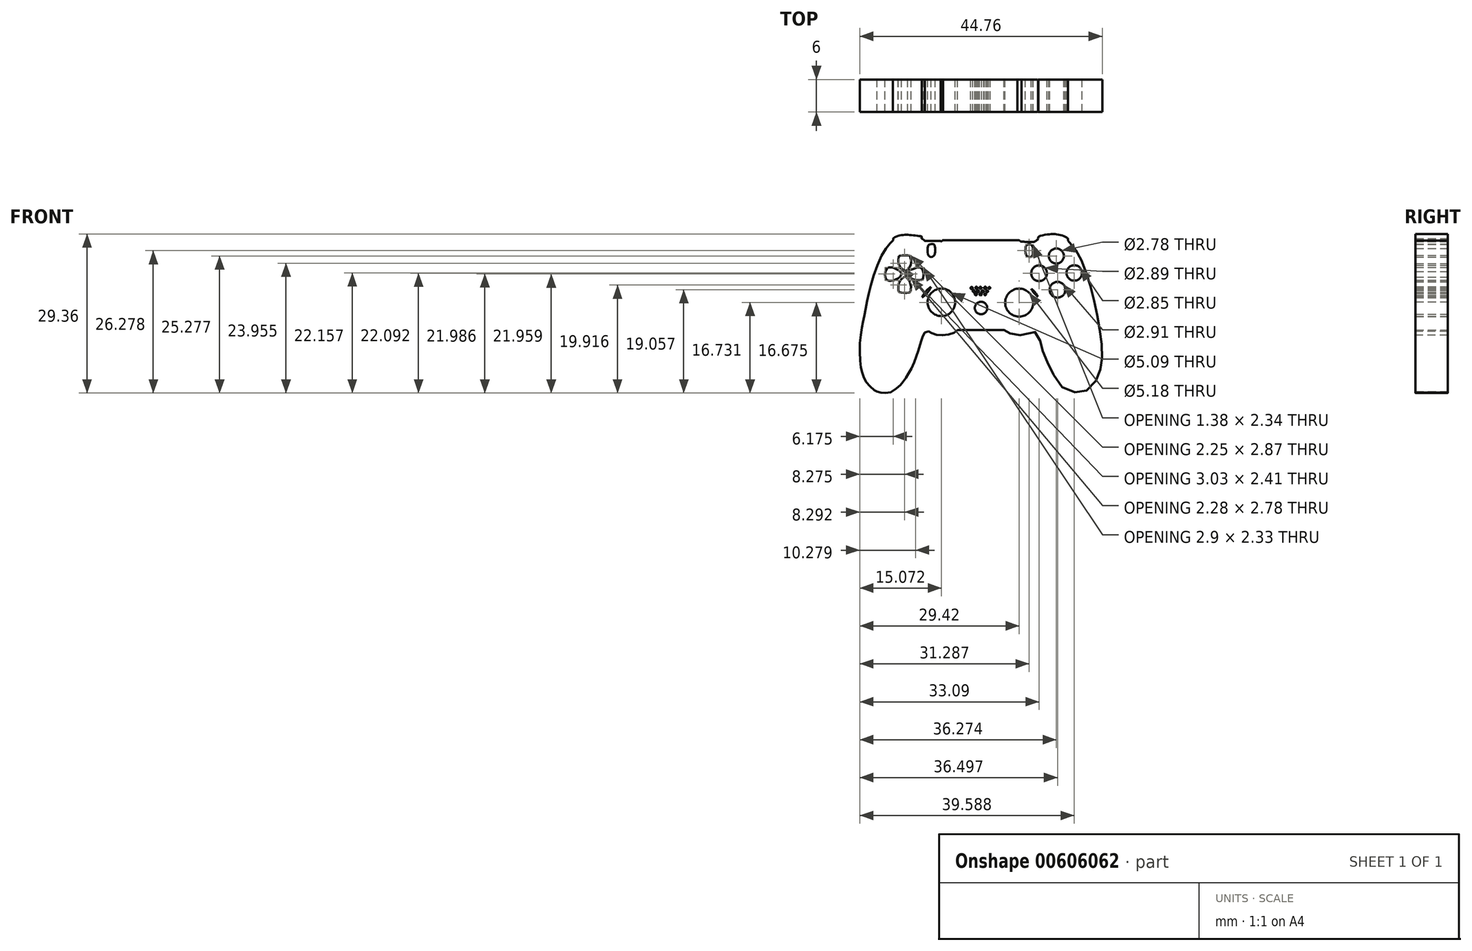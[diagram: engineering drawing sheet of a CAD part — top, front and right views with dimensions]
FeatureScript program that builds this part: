
annotation { "Feature Type Name" : "Feature", "Feature Type Description" : "" }
export const myFeature = defineFeature(function(context is Context, id is Id, definition is map)
    precondition{}
    {
        {
            var Q0;
            Q0=qCreatedBy(makeId("Front.planeOp"),FACE);
            var sketch = newSketch(context, id + "F0", { "sketchPlane" : qUnion([Q0])});
            skFitSpline(sketch, "E0", {"points": [v(11.67, 8.48) * mm, v(11.11, 8.8) * mm, v(9.77, 10.08) * mm, v(9.07, 11.57) * mm, v(8.73, 12.76) * mm, v(8.47, 16.23) * mm, v(8.78, 19.97) * mm, v(9.18, 21.94) * mm, v(9.76, 24.84) * mm, v(10.63, 28.56) * mm, v(12.8, 34.17) * mm, v(14.32, 36.12) * mm, v(14.98, 36.64) * mm, v(16, 37) * mm, v(17.62, 37.09) * mm, v(19.46, 36.87) * mm, v(20.12, 36.63) * mm, v(20.5, 36.3) * mm], "startDerivative": vector(-18.45, 2.92) * mm, "endDerivative": vector(11.5, -12.44) * mm});
            skFitSpline(sketch, "E1", {"points": [v(20.5, 36.3) * mm, v(23.4, 36.3) * mm], "startDerivative": vector(3.01, 0) * mm, "endDerivative": vector(3.01, 0) * mm});
            skFitSpline(sketch, "E2", {"points": [v(23.4, 36.3) * mm, v(23.82, 36.46) * mm], "startDerivative": vector(0.4, -0.48) * mm, "endDerivative": vector(0.31, 0.18) * mm});
            skLineSegment(sketch, "E3", {"start": v(23.82, 36.46) * mm, "end": v(37.6, 36.46) * mm});
            skFitSpline(sketch, "E4", {"points": [v(37.6, 36.46) * mm, v(38.35, 36.22) * mm], "startDerivative": vector(1.6, 0.03) * mm, "endDerivative": vector(1.1, 0.2) * mm});
            skFitSpline(sketch, "E5", {"points": [v(38.35, 36.22) * mm, v(40.82, 36.22) * mm, v(41.45, 36.68) * mm, v(43.77, 37.02) * mm, v(46.14, 36.77) * mm, v(47.69, 35.64) * mm, v(48.65, 34.04) * mm, v(49.36, 32.8) * mm, v(50.13, 30.79) * mm, v(50.8, 28.81) * mm, v(51.51, 26.15) * mm, v(52.19, 23.38) * mm, v(52.54, 21.15) * mm, v(52.94, 18.57) * mm, v(53.22, 16.06) * mm, v(53.13, 13.9) * mm, v(52.85, 12.5) * mm, v(52.31, 10.95) * mm, v(50.93, 9.07) * mm, v(49.41, 8.37) * mm, v(47.47, 8.5) * mm, v(45.46, 9.67) * mm, v(44.05, 11.97) * mm, v(43.06, 14.05) * mm, v(42.43, 15.53) * mm, v(42, 16.9) * mm, v(41.62, 18.35) * mm, v(40.95, 19.41) * mm, v(40.55, 19.61) * mm, v(40.08, 19.46) * mm, v(39.08, 19.02) * mm, v(38.35, 18.91) * mm, v(37.21, 18.94) * mm, v(36.04, 19.31) * mm, v(35.5, 19.52) * mm, v(35.06, 19.9) * mm], "startDerivative": vector(85.73, -8.47) * mm, "endDerivative": vector(-25.77, 24.87) * mm});
            skLineSegment(sketch, "E6", {"start": v(35.06, 19.9) * mm, "end": v(26.53, 19.9) * mm});
            skFitSpline(sketch, "E7", {"points": [v(26.53, 19.9) * mm, v(25.8, 19.32) * mm, v(24.43, 18.94) * mm, v(22.8, 18.95) * mm, v(21.78, 19.28) * mm, v(21.27, 19.58) * mm, v(20.71, 19.6) * mm, v(20.21, 19) * mm, v(19.94, 18.29) * mm, v(19.7, 17.43) * mm, v(19.26, 16.05) * mm, v(18.73, 14.5) * mm, v(18.06, 12.88) * mm, v(17.29, 11.57) * mm, v(16.86, 10.81) * mm, v(16.29, 10.06) * mm, v(15.75, 9.51) * mm, v(14.38, 8.48) * mm, v(13.06, 8.26) * mm, v(12.31, 8.34) * mm, v(11.67, 8.48) * mm], "startDerivative": vector(-13.72, -13.36) * mm, "endDerivative": vector(-13, 6.23) * mm});
            skCircle(sketch, "E8", {"center": v(16.9, 30.17) * mm, "radius": 5.27 * mm});
            skPoint(sketch, "E8.first.point", {"position": v(15.62, 35.28) * mm});
            skPoint(sketch, "E8.second.point", {"position": v(17.87, 24.98) * mm});
            skPoint(sketch, "E8.third.point", {"position": v(22.06, 29.02) * mm});
            skCircle(sketch, "E9", {"center": v(23.65, 24.44) * mm, "radius": 3.95 * mm});
            skPoint(sketch, "E9.first.point", {"position": v(20.6, 26.94) * mm});
            skPoint(sketch, "E9.second.point", {"position": v(26.57, 21.78) * mm});
            skPoint(sketch, "E9.third.point", {"position": v(27.55, 25.07) * mm});
            skCircle(sketch, "E10", {"center": v(30.85, 23.93) * mm, "radius": 1.15 * mm});
            skPoint(sketch, "E10.first.point", {"position": v(29.9, 24.57) * mm});
            skPoint(sketch, "E10.second.point", {"position": v(31.76, 23.23) * mm});
            skPoint(sketch, "E10.third.point", {"position": v(30.4, 22.87) * mm});
            skCircle(sketch, "E11", {"center": v(37.8, 24.25) * mm, "radius": 3.97 * mm});
            skPoint(sketch, "E11.first.point", {"position": v(33.93, 25.07) * mm});
            skPoint(sketch, "E11.second.point", {"position": v(41.7, 23.5) * mm});
            skPoint(sketch, "E11.third.point", {"position": v(38.32, 28.19) * mm});
            skCircle(sketch, "E12", {"center": v(44.63, 30.1) * mm, "radius": 5.23 * mm});
            skPoint(sketch, "E12.first.point", {"position": v(41.57, 34.35) * mm});
            skPoint(sketch, "E12.second.point", {"position": v(47.68, 25.85) * mm});
            skPoint(sketch, "E12.third.point", {"position": v(48.08, 34.03) * mm});
            skCircle(sketch, "E13", {"center": v(44.74, 33.53) * mm, "radius": 1.4 * mm});
            skPoint(sketch, "E13.first.point", {"position": v(44.01, 32.34) * mm});
            skPoint(sketch, "E13.second.point", {"position": v(45.57, 34.65) * mm});
            skPoint(sketch, "E13.third.point", {"position": v(44.01, 34.71) * mm});
            skCircle(sketch, "E14", {"center": v(41.56, 30.34) * mm, "radius": 1.45 * mm});
            skPoint(sketch, "E14.first.point", {"position": v(40.34, 31.12) * mm});
            skPoint(sketch, "E14.second.point", {"position": v(42.8, 29.6) * mm});
            skPoint(sketch, "E14.third.point", {"position": v(41.96, 31.73) * mm});
            skCircle(sketch, "E15", {"center": v(48.06, 30.4) * mm, "radius": 1.43 * mm});
            skPoint(sketch, "E15.first.point", {"position": v(46.63, 30.34) * mm});
            skPoint(sketch, "E15.second.point", {"position": v(49.48, 30.49) * mm});
            skPoint(sketch, "E15.third.point", {"position": v(47.61, 31.76) * mm});
            skCircle(sketch, "E16", {"center": v(44.97, 27.3) * mm, "radius": 1.45 * mm});
            skPoint(sketch, "E16.first.point", {"position": v(43.84, 28.23) * mm});
            skPoint(sketch, "E16.second.point", {"position": v(46.07, 26.36) * mm});
            skPoint(sketch, "E16.third.point", {"position": v(44.88, 25.86) * mm});
            skCircle(sketch, "E17", {"center": v(37.9, 24.93) * mm, "radius": 2.59 * mm});
            skPoint(sketch, "E17.first.point", {"position": v(36, 26.7) * mm});
            skPoint(sketch, "E17.second.point", {"position": v(39.94, 23.35) * mm});
            skPoint(sketch, "E17.third.point", {"position": v(40.12, 26.24) * mm});
            skCircle(sketch, "E18", {"center": v(23.54, 24.98) * mm, "radius": 2.55 * mm});
            skPoint(sketch, "E18.first.point", {"position": v(21.68, 23.25) * mm});
            skPoint(sketch, "E18.second.point", {"position": v(25.47, 26.64) * mm});
            skPoint(sketch, "E18.third.point", {"position": v(22.33, 27.22) * mm});
            skFitSpline(sketch, "E19", {"points": [v(37.6, 36.46) * mm, v(37.98, 36.22) * mm, v(38.2, 35.62) * mm, v(38.12, 29.3) * mm, v(37.98, 28.86) * mm, v(37.6, 28.65) * mm, v(35.07, 28.6) * mm, v(31.65, 28.65) * mm, v(28.05, 28.65) * mm, v(24.57, 28.65) * mm, v(23.8, 28.77) * mm, v(23.35, 29.13) * mm, v(23.2, 30.85) * mm, v(23.26, 34.5) * mm, v(23.3, 35.85) * mm, v(23.53, 36.25) * mm], "startDerivative": vector(12.31, -6.87) * mm, "endDerivative": vector(7.88, 9.78) * mm});
            skFitSpline(sketch, "E20", {"points": [v(21.05, 35.3) * mm, v(21.35, 35.67) * mm, v(22, 35.74) * mm, v(22.33, 35.31) * mm, v(22.33, 33.92) * mm, v(21.78, 33.37) * mm, v(21.12, 33.69) * mm, v(21.05, 35.3) * mm]});
            skFitSpline(sketch, "E21", {"points": [v(40.35, 33.6) * mm, v(40.16, 33.38) * mm, v(39.51, 33.42) * mm, v(39.16, 33.8) * mm, v(39.14, 35.3) * mm, v(39.54, 35.67) * mm, v(40.02, 35.67) * mm, v(40.39, 35.23) * mm, v(40.35, 33.6) * mm]});
            skFitSpline(sketch, "E22", {"points": [v(41.45, 36.68) * mm, v(41.45, 37.05) * mm, v(43.52, 37.56) * mm, v(44.63, 37.58) * mm, v(46.24, 37.15) * mm, v(46.9, 36.68) * mm, v(46.87, 36.4) * mm], "startDerivative": vector(-1.5, 3.76) * mm, "endDerivative": vector(-1.19, -3.07) * mm});
            skFitSpline(sketch, "E23", {"points": [v(14.64, 36.42) * mm, v(14.65, 36.77) * mm, v(15.51, 37.23) * mm, v(16.75, 37.44) * mm, v(18.05, 37.4) * mm, v(19.54, 37.21) * mm, v(19.9, 37.1) * mm, v(19.83, 36.77) * mm], "startDerivative": vector(-1, 3.85) * mm, "endDerivative": vector(-1.83, -4.28) * mm});
            skFitSpline(sketch, "E24", {"points": [v(15.64, 32.09) * mm, v(15.68, 33.4) * mm, v(15.86, 33.6) * mm, v(17.56, 33.58) * mm, v(17.8, 33.37) * mm, v(17.86, 31.92) * mm, v(16.94, 30.73) * mm, v(16.64, 30.71) * mm, v(15.64, 32.09) * mm]});
            skFitSpline(sketch, "E25", {"points": [v(17.3, 30.4) * mm, v(18.45, 31.2) * mm, v(19.94, 31.2) * mm, v(20.12, 29.34) * mm, v(19.83, 29.13) * mm, v(18.4, 29.2) * mm, v(17.3, 30.4) * mm]});
            skFitSpline(sketch, "E26", {"points": [v(13.5, 31.24) * mm, v(14.88, 31.25) * mm, v(16.16, 30.25) * mm, v(14.97, 29.14) * mm, v(13.32, 29.28) * mm, v(13.5, 31.24) * mm]});
            skFitSpline(sketch, "E27", {"points": [v(15.73, 28.57) * mm, v(16.56, 29.6) * mm, v(16.94, 29.65) * mm, v(17.81, 28.46) * mm, v(17.84, 27) * mm, v(17.61, 26.8) * mm, v(15.83, 26.81) * mm, v(15.64, 27.03) * mm, v(15.73, 28.57) * mm]});
            skCircle(sketch, "E28", {"center": v(48.1, 30.53) * mm, "radius": 0.92 * mm});
            skPoint(sketch, "E28.first.point", {"position": v(47.4, 31.13) * mm});
            skPoint(sketch, "E28.second.point", {"position": v(48.75, 29.9) * mm});
            skPoint(sketch, "E28.third.point", {"position": v(48.66, 31.25) * mm});
            skLineSegment(sketch, "E29.bottom", {"start": v(42.32, 29.79) * mm, "end": v(40.81, 29.79) * mm});
            skLineSegment(sketch, "E29.top", {"start": v(42.32, 31.13) * mm, "end": v(40.81, 31.13) * mm});
            skLineSegment(sketch, "E29.left", {"start": v(42.32, 29.79) * mm, "end": v(42.32, 31.13) * mm});
            skLineSegment(sketch, "E29.right", {"start": v(40.81, 29.79) * mm, "end": v(40.81, 31.13) * mm});
            skPoint(sketch, "E29.middle", {"position": v(41.57, 30.46) * mm});
            skLineSegment(sketch, "E30", {"start": v(43.9, 33.23) * mm, "end": v(45.53, 33.23) * mm});
            skLineSegment(sketch, "E31", {"start": v(45.53, 33.23) * mm, "end": v(44.73, 34.53) * mm});
            skLineSegment(sketch, "E32", {"start": v(44.73, 34.53) * mm, "end": v(43.9, 33.23) * mm});
            skLineSegment(sketch, "E33", {"start": v(44.28, 27.82) * mm, "end": v(45.62, 26.52) * mm});
            skLineSegment(sketch, "E34", {"start": v(44.23, 26.5) * mm, "end": v(45.6, 27.73) * mm});
            skCircle(sketch, "E35", {"center": v(29.13, 27.63) * mm, "radius": 0.2 * mm});
            skPoint(sketch, "E35.first.point", {"position": v(28.98, 27.78) * mm});
            skPoint(sketch, "E35.second.point", {"position": v(29.25, 27.46) * mm});
            skPoint(sketch, "E35.third.point", {"position": v(29.23, 27.8) * mm});
            skCircle(sketch, "E36", {"center": v(30, 27.65) * mm, "radius": 0.2 * mm});
            skPoint(sketch, "E36.first.point", {"position": v(29.84, 27.79) * mm});
            skPoint(sketch, "E36.second.point", {"position": v(30.15, 27.53) * mm});
            skPoint(sketch, "E36.third.point", {"position": v(30.14, 27.78) * mm});
            skCircle(sketch, "E37", {"center": v(30.75, 27.66) * mm, "radius": 0.2 * mm});
            skPoint(sketch, "E37.first.point", {"position": v(30.6, 27.79) * mm});
            skPoint(sketch, "E37.second.point", {"position": v(30.9, 27.54) * mm});
            skPoint(sketch, "E37.third.point", {"position": v(30.88, 27.8) * mm});
            skCircle(sketch, "E38", {"center": v(31.61, 27.65) * mm, "radius": 0.2 * mm});
            skPoint(sketch, "E38.first.point", {"position": v(31.47, 27.8) * mm});
            skPoint(sketch, "E38.second.point", {"position": v(31.77, 27.51) * mm});
            skPoint(sketch, "E38.third.point", {"position": v(31.75, 27.8) * mm});
            skCircle(sketch, "E39", {"center": v(32.38, 27.64) * mm, "radius": 0.18 * mm});
            skPoint(sketch, "E39.first.point", {"position": v(32.29, 27.8) * mm});
            skPoint(sketch, "E39.second.point", {"position": v(32.47, 27.49) * mm});
            skPoint(sketch, "E39.third.point", {"position": v(32.55, 27.69) * mm});
            skCircle(sketch, "E40", {"center": v(31.96, 27.02) * mm, "radius": 0.19 * mm});
            skPoint(sketch, "E40.first.point", {"position": v(31.87, 27.18) * mm});
            skPoint(sketch, "E40.second.point", {"position": v(32.08, 26.86) * mm});
            skPoint(sketch, "E40.third.point", {"position": v(32.14, 27.07) * mm});
            skCircle(sketch, "E41", {"center": v(31.15, 27.02) * mm, "radius": 0.18 * mm});
            skPoint(sketch, "E41.first.point", {"position": v(31.04, 27.15) * mm});
            skPoint(sketch, "E41.second.point", {"position": v(31.26, 26.88) * mm});
            skPoint(sketch, "E41.third.point", {"position": v(31.32, 27.09) * mm});
            skCircle(sketch, "E42", {"center": v(30.29, 27.03) * mm, "radius": 0.19 * mm});
            skPoint(sketch, "E42.first.point", {"position": v(30.17, 27.17) * mm});
            skPoint(sketch, "E42.second.point", {"position": v(30.41, 26.9) * mm});
            skPoint(sketch, "E42.third.point", {"position": v(30.43, 27.15) * mm});
            skCircle(sketch, "E43", {"center": v(29.52, 27.02) * mm, "radius": 0.19 * mm});
            skPoint(sketch, "E43.first.point", {"position": v(29.4, 27.16) * mm});
            skPoint(sketch, "E43.second.point", {"position": v(29.65, 26.89) * mm});
            skPoint(sketch, "E43.third.point", {"position": v(29.7, 27.09) * mm});
            skCircle(sketch, "E44", {"center": v(29.89, 26.48) * mm, "radius": 0.2 * mm});
            skPoint(sketch, "E44.first.point", {"position": v(29.75, 26.62) * mm});
            skPoint(sketch, "E44.second.point", {"position": v(30.04, 26.37) * mm});
            skPoint(sketch, "E44.third.point", {"position": v(30.08, 26.54) * mm});
            skCircle(sketch, "E45", {"center": v(30.78, 26.46) * mm, "radius": 0.2 * mm});
            skPoint(sketch, "E45.first.point", {"position": v(30.62, 26.6) * mm});
            skPoint(sketch, "E45.second.point", {"position": v(30.92, 26.3) * mm});
            skPoint(sketch, "E45.third.point", {"position": v(30.93, 26.6) * mm});
            skCircle(sketch, "E46", {"center": v(31.62, 26.47) * mm, "radius": 0.17 * mm});
            skPoint(sketch, "E46.first.point", {"position": v(31.49, 26.57) * mm});
            skPoint(sketch, "E46.second.point", {"position": v(31.72, 26.33) * mm});
            skPoint(sketch, "E46.third.point", {"position": v(31.75, 26.57) * mm});
            skLineSegment(sketch, "E47", {"start": v(23.54, 36.14) * mm, "end": v(37.98, 36.15) * mm});
            skSolve(sketch);
        }
        {
            var Q0;
            Q0 = qSketchRegion(id + "F0", true);
            var Q1;
            Q1=makeQuery(id+"F0.imprint","IMPRINT",FACE,{"disambiguationData":[TD([[makeQuery(id+"F0.imprint","IMPRINT",EDGE,{"derivedFrom":sQuery(id+"F0.wireOp",EDGE,"E18")}),-1.0]])]});
            var Q2;
            Q2=makeQuery(id+"F0.imprint","IMPRINT",FACE,{"disambiguationData":[TD([[makeQuery(id+"F0.imprint","IMPRINT",EDGE,{"derivedFrom":sQuery(id+"F0.wireOp",EDGE,"E24")}),1.0]])]});
            var Q3;
            Q3=makeQuery(id+"F0.imprint","IMPRINT",FACE,{"disambiguationData":[TD([[makeQuery(id+"F0.imprint","IMPRINT",EDGE,{"derivedFrom":sQuery(id+"F0.wireOp",EDGE,"E17")}),-1.0]])]});
            var Q4;
            Q4=makeQuery(id+"F0.imprint","IMPRINT",FACE,{"disambiguationData":[TD([[makeQuery(id+"F0.imprint","IMPRINT",EDGE,{"derivedFrom":sQuery(id+"F0.wireOp",EDGE,"E13")}),-1.0]])]});
            extrude(context, id + "F1", {"entities" : qUnion([Q0, Q1, Q2, Q3, Q4]), "depth" : 6 * mm, "offsetDistance" : 25 * mm});
        }
    });
